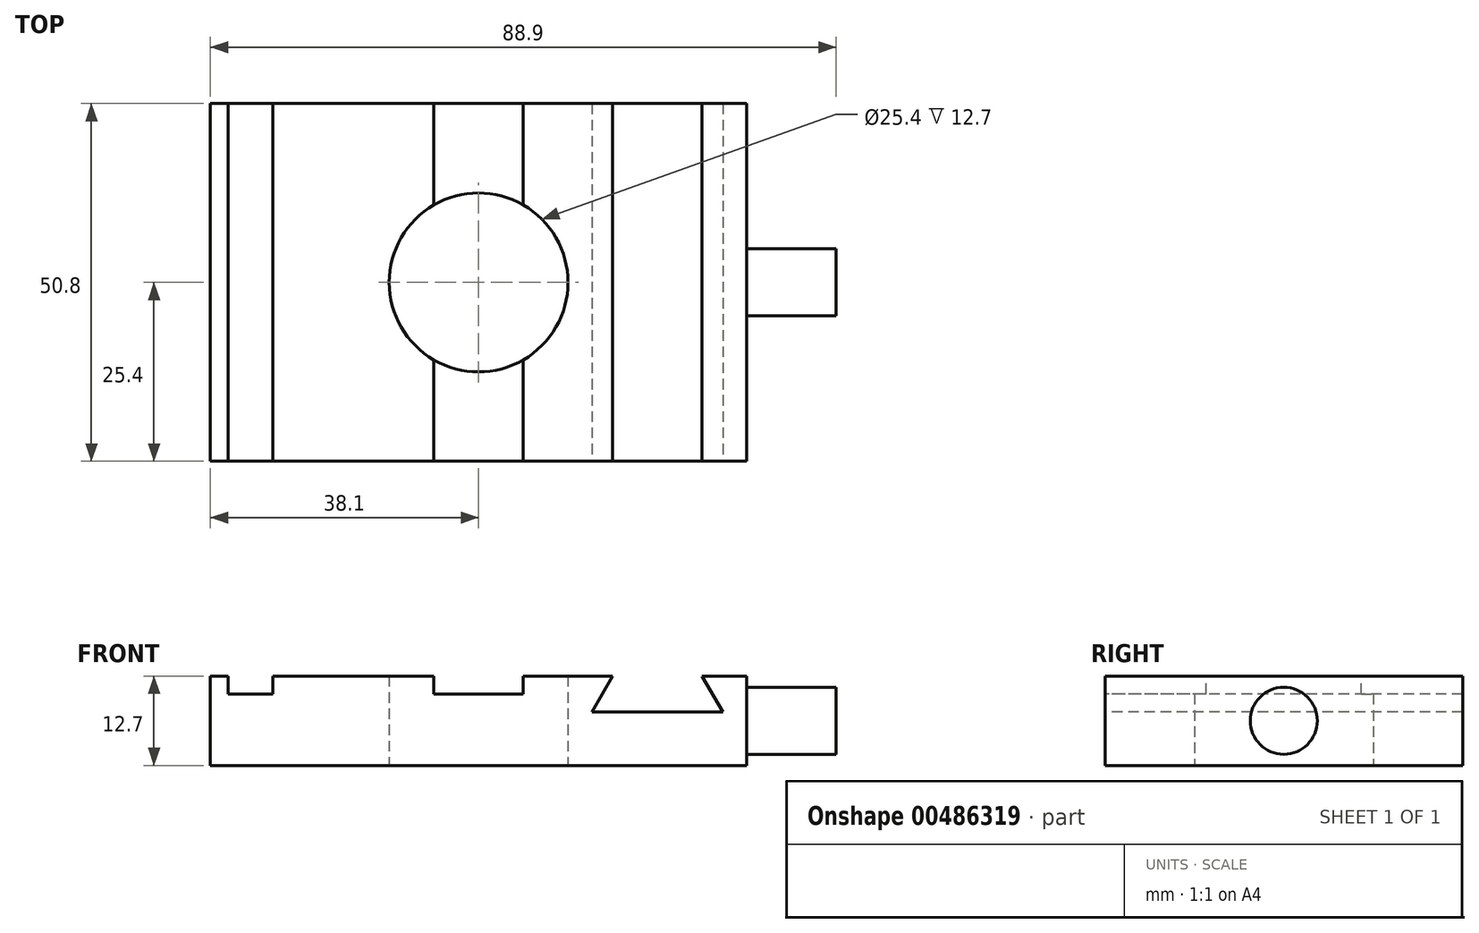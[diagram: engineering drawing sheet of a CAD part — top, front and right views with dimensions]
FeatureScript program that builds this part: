
annotation { "Feature Type Name" : "Feature", "Feature Type Description" : "" }
export const myFeature = defineFeature(function(context is Context, id is Id, definition is map)
    precondition{}
    {
        {
            var Q0;
            Q0=qCreatedBy(makeId("Top.planeOp"),FACE);
            var sketch = newSketch(context, id + "F0", { "sketchPlane" : qUnion([Q0])});
            skLineSegment(sketch, "E0.bottom", {"start": v(38.1, 25.4) * mm, "end": v(-38.1, 25.4) * mm});
            skLineSegment(sketch, "E0.top", {"start": v(38.1, -25.4) * mm, "end": v(-38.1, -25.4) * mm});
            skLineSegment(sketch, "E0.left", {"start": v(38.1, 25.4) * mm, "end": v(38.1, -25.4) * mm});
            skLineSegment(sketch, "E0.right", {"start": v(-38.1, 25.4) * mm, "end": v(-38.1, -25.4) * mm});
            skPoint(sketch, "E0.middle", {"position": v(0, 0) * mm});
            skCircle(sketch, "E1", {"center": v(0, 0) * mm, "radius": 12.7 * mm});
            skSolve(sketch);
        }
        {
            var Q0;
            Q0 = qSketchRegion(id + "F0", true);
            extrude(context, id + "F1", {"entities" : qUnion([Q0]), "depth" : 12.7 * mm, "offsetDistance" : 25.4 * mm});
        }
        {
            var Q0;
            Q0=makeQuery(id+"F1.opExtrude","CAP_FACE",FACE,{"disambiguationData":[OSD([sQuery(id+"F0.wireOp",EDGE,"E0.bottom"),sQuery(id+"F0.wireOp",EDGE,"E0.top"),sQuery(id+"F0.wireOp",EDGE,"E0.left"),sQuery(id+"F0.wireOp",EDGE,"E0.right"),sQuery(id+"F0.wireOp",EDGE,"E1")])],"isStart":false});
            var sketch = newSketch(context, id + "F2", { "sketchPlane" : qUnion([Q0])});
            skLineSegment(sketch, "E2.bottom", {"start": v(-35.56, 25.4) * mm, "end": v(-29.2, 25.4) * mm});
            skLineSegment(sketch, "E2.top", {"start": v(-35.56, -25.4) * mm, "end": v(-29.2, -25.4) * mm});
            skLineSegment(sketch, "E2.left", {"start": v(-35.56, 25.4) * mm, "end": v(-35.56, -25.4) * mm});
            skLineSegment(sketch, "E2.right", {"start": v(-29.2, 25.4) * mm, "end": v(-29.2, -25.4) * mm});
            skLineSegment(sketch, "E3.bottom", {"start": v(-6.35, 25.4) * mm, "end": v(6.35, 25.4) * mm});
            skLineSegment(sketch, "E3.top", {"start": v(-6.35, -25.4) * mm, "end": v(6.35, -25.4) * mm});
            skLineSegment(sketch, "E4", {"start": v(0, -25.4) * mm, "end": v(0, 25.4) * mm, "construction": true});
            skLineSegment(sketch, "E5", {"start": v(-6.35, 25.4) * mm, "end": v(-6.35, -25.4) * mm});
            skLineSegment(sketch, "E6", {"start": v(6.35, 25.4) * mm, "end": v(6.35, -25.4) * mm});
            skSolve(sketch);
        }
        {
            var Q0;
            Q0=makeQuery(id+"F2.imprint","IMPRINT",FACE,{"disambiguationData":[TD([[makeQuery(id+"F2.imprint","IMPRINT",EDGE,{"derivedFrom":sQuery(id+"F2.wireOp",EDGE,"E2.bottom")}),1.0]])]});
            var Q1;
            {var subQ0=sQuery(id+"F2.wireOp",EDGE,"E3.top");Q1=makeQuery(id+"F2.imprint","IMPRINT",FACE,{"disambiguationData":[TD([[makeQuery(id+"F2.imprint","IMPRINT",EDGE,{"derivedFrom":subQ0}),-1.0]])]});}
            var Q2;
            {var subQ0=sQuery(id+"F2.wireOp",EDGE,"E3.bottom");Q2=makeQuery(id+"F2.imprint","IMPRINT",FACE,{"disambiguationData":[TD([[makeQuery(id+"F2.imprint","IMPRINT",EDGE,{"derivedFrom":subQ0}),1.0]])]});}
            extrude(context, id + "F3", {"entities" : qUnion([Q0, Q1, Q2]), "operationType" : NewBodyOperationType.REMOVE, "oppositeDirection" : true, "depth" : 2.54 * mm, "offsetDistance" : 25.4 * mm});
        }
        {
            var Q0;
            Q0=makeQuery(id+"F1.opExtrude","SWEPT_FACE",FACE,{"disambiguationData":[OSD([sQuery(id+"F0.wireOp",EDGE,"E0.top")])]});
            var sketch = newSketch(context, id + "F4", { "sketchPlane" : qUnion([Q0])});
            skLineSegment(sketch, "E7", {"start": v(19.05, 12.7) * mm, "end": v(16.12, 7.62) * mm});
            skLineSegment(sketch, "E8", {"start": v(16.12, 7.62) * mm, "end": v(34.68, 7.62) * mm});
            skLineSegment(sketch, "E9", {"start": v(34.68, 7.62) * mm, "end": v(31.75, 12.7) * mm});
            skLineSegment(sketch, "E10", {"start": v(31.75, 12.7) * mm, "end": v(19.05, 12.7) * mm});
            skLineSegment(sketch, "E11", {"start": v(25.4, 7.62) * mm, "end": v(25.4, 12.7) * mm, "construction": true});
            skSolve(sketch);
        }
        {
            var Q0;
            Q0=makeQuery(id+"F4.imprint","IMPRINT",FACE,{"disambiguationData":[TD([[makeQuery(id+"F4.imprint","IMPRINT",EDGE,{"derivedFrom":sQuery(id+"F4.wireOp",EDGE,"E7")}),1.0]])]});
            extrude(context, id + "F5", {"entities" : qUnion([Q0]), "operationType" : NewBodyOperationType.REMOVE, "endBound" : BoundingType.THROUGH_ALL, "oppositeDirection" : true, "depth" : 25.4 * mm, "offsetDistance" : 25.4 * mm});
        }
        {
            var Q0;
            Q0=makeQuery(id+"F1.opExtrude","SWEPT_FACE",FACE,{"disambiguationData":[OSD([sQuery(id+"F0.wireOp",EDGE,"E0.left")])]});
            var sketch = newSketch(context, id + "F6", { "sketchPlane" : qUnion([Q0])});
            skCircle(sketch, "E12", {"center": v(0, 6.35) * mm, "radius": 4.76 * mm});
            skPoint(sketch, "E12.centerSnap0", {"position": v(0, 12.7) * mm});
            skPoint(sketch, "E12.centerSnap1", {"position": v(-25.4, 6.35) * mm});
            skSolve(sketch);
        }
        {
            var Q0;
            Q0=makeQuery(id+"F6.imprint","IMPRINT",FACE,{"disambiguationData":[TD([[makeQuery(id+"F6.imprint","IMPRINT",EDGE,{"derivedFrom":sQuery(id+"F6.wireOp",EDGE,"E12")}),1.0]])]});
            extrude(context, id + "F7", {"entities" : qUnion([Q0]), "operationType" : NewBodyOperationType.ADD, "depth" : 12.7 * mm, "offsetDistance" : 25.4 * mm});
        }
    });
